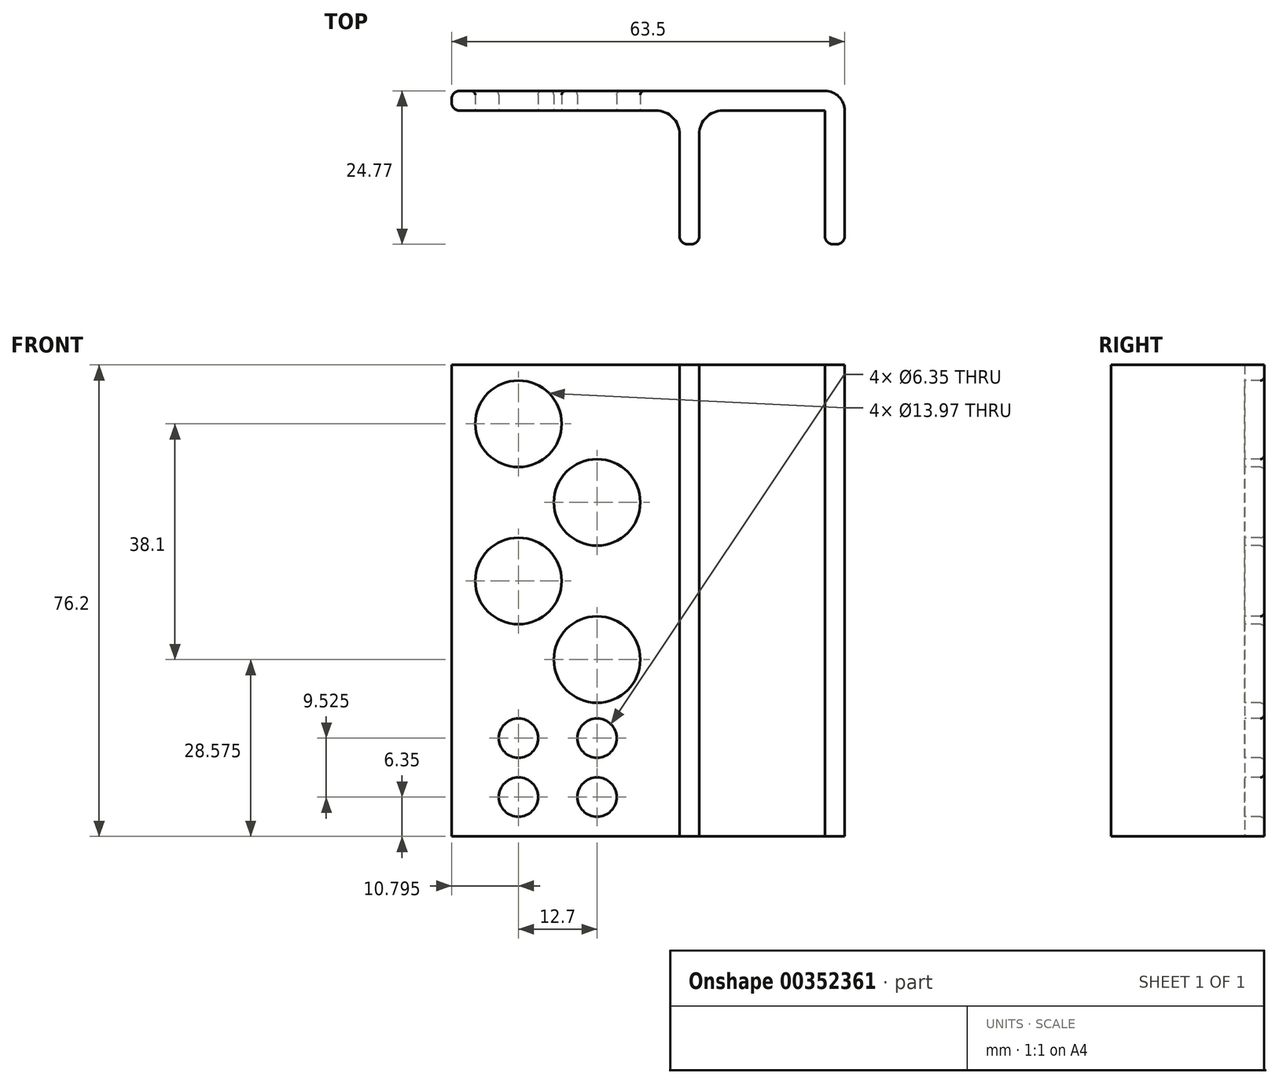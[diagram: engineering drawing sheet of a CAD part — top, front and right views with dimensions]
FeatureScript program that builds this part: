
annotation { "Feature Type Name" : "Feature", "Feature Type Description" : "" }
export const myFeature = defineFeature(function(context is Context, id is Id, definition is map)
    precondition{}
    {
        {
            var Q0;
            Q0=qCreatedBy(makeId("Top.planeOp"),FACE);
            var sketch = newSketch(context, id + "F0", { "sketchPlane" : qUnion([Q0])});
            skLineSegment(sketch, "E0.bottom", {"start": v(28.57, 1.59) * mm, "end": v(-30.48, 1.59) * mm});
            skLineSegment(sketch, "E0.top", {"start": v(28.57, -1.59) * mm, "end": v(12.06, -1.59) * mm});
            skLineSegment(sketch, "E0.left", {"start": v(31.75, -1.59) * mm, "end": v(31.75, -1.59) * mm});
            skLineSegment(sketch, "E0.right", {"start": v(-31.75, 0.32) * mm, "end": v(-31.75, -0.32) * mm});
            skPoint(sketch, "E0.middle", {"position": v(0, 0) * mm});
            skLineSegment(sketch, "E1", {"start": v(31.75, -1.59) * mm, "end": v(31.75, -21.9) * mm});
            skLineSegment(sketch, "E2", {"start": v(30.48, -23.18) * mm, "end": v(29.85, -23.18) * mm});
            skLineSegment(sketch, "E3", {"start": v(28.58, -21.9) * mm, "end": v(28.57, -1.59) * mm});
            skLineSegment(sketch, "E4", {"start": v(5.08, -5.4) * mm, "end": v(5.08, -21.9) * mm});
            skLineSegment(sketch, "E5", {"start": v(6.35, -23.18) * mm, "end": v(6.98, -23.18) * mm});
            skLineSegment(sketch, "E6", {"start": v(8.25, -21.9) * mm, "end": v(8.25, -5.4) * mm});
            skLineSegment(sketch, "E7.trimOffspring", {"start": v(1.27, -1.59) * mm, "end": v(-30.48, -1.59) * mm});
            skPoint(sketch, "E8.visualSharp", {"position": v(8.25, -1.59) * mm});
            skArc(sketch, "E8.filletArc", {"start": v(12.06, -1.59) * mm, "mid": v(9.37, -2.7) * mm, "end": v(8.25, -5.4) * mm});
            skPoint(sketch, "E9.visualSharp", {"position": v(5.08, -1.59) * mm});
            skArc(sketch, "E9.filletArc", {"start": v(5.08, -5.4) * mm, "mid": v(3.96, -2.7) * mm, "end": v(1.27, -1.59) * mm});
            skPoint(sketch, "E10.visualSharp", {"position": v(5.08, -23.18) * mm});
            skArc(sketch, "E10.filletArc", {"start": v(5.08, -21.9) * mm, "mid": v(5.45, -22.8) * mm, "end": v(6.35, -23.18) * mm});
            skPoint(sketch, "E11.visualSharp", {"position": v(8.25, -23.18) * mm});
            skArc(sketch, "E11.filletArc", {"start": v(6.98, -23.18) * mm, "mid": v(7.88, -22.8) * mm, "end": v(8.26, -21.9) * mm});
            skPoint(sketch, "E12.visualSharp", {"position": v(28.58, -23.18) * mm});
            skArc(sketch, "E12.filletArc", {"start": v(28.57, -21.9) * mm, "mid": v(28.95, -22.8) * mm, "end": v(29.85, -23.18) * mm});
            skPoint(sketch, "E13.visualSharp", {"position": v(31.75, -23.18) * mm});
            skArc(sketch, "E13.filletArc", {"start": v(30.48, -23.18) * mm, "mid": v(31.38, -22.8) * mm, "end": v(31.75, -21.9) * mm});
            skPoint(sketch, "E14.visualSharp", {"position": v(-31.75, 1.59) * mm});
            skArc(sketch, "E14.filletArc", {"start": v(-30.48, 1.59) * mm, "mid": v(-31.38, 1.22) * mm, "end": v(-31.75, 0.32) * mm});
            skPoint(sketch, "E15.visualSharp", {"position": v(-31.75, -1.59) * mm});
            skArc(sketch, "E15.filletArc", {"start": v(-31.75, -0.32) * mm, "mid": v(-31.38, -1.22) * mm, "end": v(-30.48, -1.59) * mm});
            skPoint(sketch, "E16.visualSharp", {"position": v(31.75, 1.59) * mm});
            skArc(sketch, "E16.filletArc", {"start": v(31.75, -1.59) * mm, "mid": v(30.82, 0.66) * mm, "end": v(28.57, 1.59) * mm});
            skSolve(sketch);
        }
        {
            var Q0;
            Q0=makeQuery(id+"F0.imprint","IMPRINT",FACE,{"disambiguationData":[TD([[makeQuery(id+"F0.imprint","IMPRINT",EDGE,{"derivedFrom":sQuery(id+"F0.wireOp",EDGE,"E0.bottom")}),1.0]])]});
            extrude(context, id + "F1", {"entities" : qUnion([Q0]), "depth" : 76.2 * mm});
        }
        {
            var Q0;
            Q0=makeQuery(id+"F1.opExtrude","SWEPT_FACE",FACE,{"disambiguationData":[OSD([sQuery(id+"F0.wireOp",EDGE,"E7.trimOffspring")])]});
            var sketch = newSketch(context, id + "F2", { "sketchPlane" : qUnion([Q0])});
            skCircle(sketch, "E17", {"center": v(-20.96, 15.88) * mm, "radius": 3.18 * mm});
            skCircle(sketch, "E18", {"center": v(-8.26, 15.88) * mm, "radius": 3.18 * mm});
            skCircle(sketch, "E19", {"center": v(-20.96, 6.35) * mm, "radius": 3.18 * mm});
            skCircle(sketch, "E20", {"center": v(-8.26, 6.35) * mm, "radius": 3.18 * mm});
            skCircle(sketch, "E21", {"center": v(-8.26, 28.58) * mm, "radius": 6.99 * mm});
            skCircle(sketch, "E22", {"center": v(-20.96, 41.28) * mm, "radius": 6.99 * mm});
            skCircle(sketch, "E23", {"center": v(-8.26, 53.98) * mm, "radius": 6.99 * mm});
            skCircle(sketch, "E24", {"center": v(-20.96, 66.68) * mm, "radius": 6.99 * mm});
            skSolve(sketch);
        }
        {
            var Q0;
            Q0 = qSketchRegion(id + "F2", true);
            extrude(context, id + "F3", {"entities" : qUnion([Q0]), "operationType" : NewBodyOperationType.REMOVE, "oppositeDirection" : true, "depth" : 25.4 * mm});
        }
        {
            var Q0;
            Q0=makeQuery(id+"F3.boolean.opBoolean","COPY",EDGE,{"derivedFrom":makeQuery(id+"F3.opExtrude","CAP_EDGE",EDGE,{"disambiguationData":[OSD([sQuery(id+"F2.wireOp",EDGE,"E24")])],"isStart":true})});
            var Q1;
            Q1=makeQuery(id+"F3.boolean.opBoolean","COPY",EDGE,{"derivedFrom":makeQuery(id+"F3.opExtrude","CAP_EDGE",EDGE,{"disambiguationData":[OSD([sQuery(id+"F2.wireOp",EDGE,"E23")])],"isStart":true})});
            var Q2;
            Q2=makeQuery(id+"F3.boolean.opBoolean","COPY",EDGE,{"derivedFrom":makeQuery(id+"F3.opExtrude","CAP_EDGE",EDGE,{"disambiguationData":[OSD([sQuery(id+"F2.wireOp",EDGE,"E22")])],"isStart":true})});
            var Q3;
            Q3=makeQuery(id+"F3.boolean.opBoolean","COPY",EDGE,{"derivedFrom":makeQuery(id+"F3.opExtrude","CAP_EDGE",EDGE,{"disambiguationData":[OSD([sQuery(id+"F2.wireOp",EDGE,"E21")])],"isStart":true})});
            var Q4;
            Q4=makeQuery(id+"F3.boolean.opBoolean","COPY",EDGE,{"derivedFrom":makeQuery(id+"F3.opExtrude","CAP_EDGE",EDGE,{"disambiguationData":[OSD([sQuery(id+"F2.wireOp",EDGE,"E18")])],"isStart":true})});
            var Q5;
            Q5=makeQuery(id+"F3.boolean.opBoolean","COPY",EDGE,{"derivedFrom":makeQuery(id+"F3.opExtrude","CAP_EDGE",EDGE,{"disambiguationData":[OSD([sQuery(id+"F2.wireOp",EDGE,"E20")])],"isStart":true})});
            var Q6;
            Q6=makeQuery(id+"F3.boolean.opBoolean","COPY",EDGE,{"derivedFrom":makeQuery(id+"F3.opExtrude","CAP_EDGE",EDGE,{"disambiguationData":[OSD([sQuery(id+"F2.wireOp",EDGE,"E19")])],"isStart":true})});
            var Q7;
            Q7=makeQuery(id+"F3.boolean.opBoolean","COPY",EDGE,{"derivedFrom":makeQuery(id+"F3.opExtrude","CAP_EDGE",EDGE,{"disambiguationData":[OSD([sQuery(id+"F2.wireOp",EDGE,"E17")])],"isStart":true})});
            var Q8;
            Q8=makeQuery(id+"F3.boolean.opBoolean","INTERSECT",EDGE,{"derivedFrom":[makeQuery(id+"F1.opExtrude","SWEPT_FACE",FACE,{"disambiguationData":[OSD([sQuery(id+"F0.wireOp",EDGE,"E0.bottom")])]}),makeQuery(id+"F3.opExtrude","SWEPT_FACE",FACE,{"disambiguationData":[OSD([sQuery(id+"F2.wireOp",EDGE,"E20")])]})]});
            var Q9;
            Q9=makeQuery(id+"F3.boolean.opBoolean","INTERSECT",EDGE,{"derivedFrom":[makeQuery(id+"F1.opExtrude","SWEPT_FACE",FACE,{"disambiguationData":[OSD([sQuery(id+"F0.wireOp",EDGE,"E0.bottom")])]}),makeQuery(id+"F3.opExtrude","SWEPT_FACE",FACE,{"disambiguationData":[OSD([sQuery(id+"F2.wireOp",EDGE,"E19")])]})]});
            var Q10;
            Q10=makeQuery(id+"F3.boolean.opBoolean","INTERSECT",EDGE,{"derivedFrom":[makeQuery(id+"F1.opExtrude","SWEPT_FACE",FACE,{"disambiguationData":[OSD([sQuery(id+"F0.wireOp",EDGE,"E0.bottom")])]}),makeQuery(id+"F3.opExtrude","SWEPT_FACE",FACE,{"disambiguationData":[OSD([sQuery(id+"F2.wireOp",EDGE,"E17")])]})]});
            var Q11;
            Q11=makeQuery(id+"F3.boolean.opBoolean","INTERSECT",EDGE,{"derivedFrom":[makeQuery(id+"F1.opExtrude","SWEPT_FACE",FACE,{"disambiguationData":[OSD([sQuery(id+"F0.wireOp",EDGE,"E0.bottom")])]}),makeQuery(id+"F3.opExtrude","SWEPT_FACE",FACE,{"disambiguationData":[OSD([sQuery(id+"F2.wireOp",EDGE,"E21")])]})]});
            var Q12;
            Q12=makeQuery(id+"F3.boolean.opBoolean","INTERSECT",EDGE,{"derivedFrom":[makeQuery(id+"F1.opExtrude","SWEPT_FACE",FACE,{"disambiguationData":[OSD([sQuery(id+"F0.wireOp",EDGE,"E0.bottom")])]}),makeQuery(id+"F3.opExtrude","SWEPT_FACE",FACE,{"disambiguationData":[OSD([sQuery(id+"F2.wireOp",EDGE,"E22")])]})]});
            var Q13;
            Q13=makeQuery(id+"F3.boolean.opBoolean","INTERSECT",EDGE,{"derivedFrom":[makeQuery(id+"F1.opExtrude","SWEPT_FACE",FACE,{"disambiguationData":[OSD([sQuery(id+"F0.wireOp",EDGE,"E0.bottom")])]}),makeQuery(id+"F3.opExtrude","SWEPT_FACE",FACE,{"disambiguationData":[OSD([sQuery(id+"F2.wireOp",EDGE,"E23")])]})]});
            var Q14;
            Q14=makeQuery(id+"F3.boolean.opBoolean","INTERSECT",EDGE,{"derivedFrom":[makeQuery(id+"F1.opExtrude","SWEPT_FACE",FACE,{"disambiguationData":[OSD([sQuery(id+"F0.wireOp",EDGE,"E0.bottom")])]}),makeQuery(id+"F3.opExtrude","SWEPT_FACE",FACE,{"disambiguationData":[OSD([sQuery(id+"F2.wireOp",EDGE,"E24")])]})]});
            var Q15;
            Q15=makeQuery(id+"F3.boolean.opBoolean","INTERSECT",EDGE,{"derivedFrom":[makeQuery(id+"F1.opExtrude","SWEPT_FACE",FACE,{"disambiguationData":[OSD([sQuery(id+"F0.wireOp",EDGE,"E0.bottom")])]}),makeQuery(id+"F3.opExtrude","SWEPT_FACE",FACE,{"disambiguationData":[OSD([sQuery(id+"F2.wireOp",EDGE,"E18")])]})]});
            fillet(context, id + "F4", {"entities" : qUnion([Q0, Q1, Q2, Q3, Q4, Q5, Q6, Q7, Q8, Q9, Q10, Q11, Q12, Q13, Q14, Q15]), "radius" : 0.64 * mm, "tangentPropagation" : true, "allowEdgeOverflow" : false});
        }
    });
